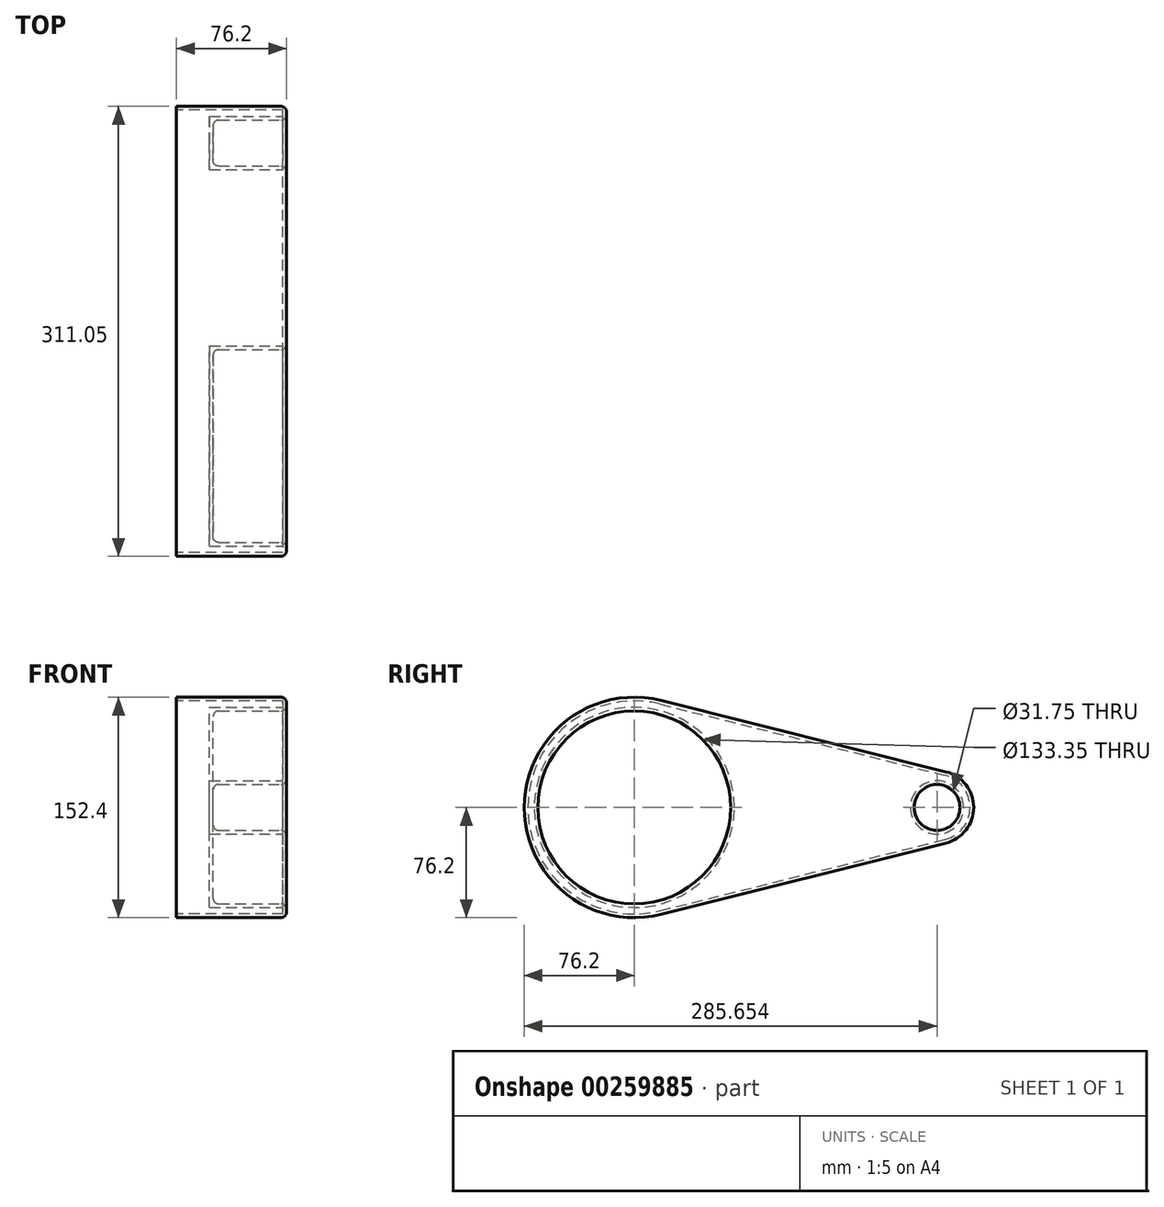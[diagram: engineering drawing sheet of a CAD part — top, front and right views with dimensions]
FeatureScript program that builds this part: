
annotation { "Feature Type Name" : "Feature", "Feature Type Description" : "" }
export const myFeature = defineFeature(function(context is Context, id is Id, definition is map)
    precondition{}
    {
        {
            var Q0;
            Q0=qCreatedBy(makeId("Right.planeOp"),FACE);
            var sketch = newSketch(context, id + "F0", { "sketchPlane" : qUnion([Q0])});
            skCircle(sketch, "E0", {"center": v(0, 0) * mm, "radius": 76.2 * mm});
            skCircle(sketch, "E1", {"center": v(209.45, 0) * mm, "radius": 25.4 * mm});
            skLineSegment(sketch, "E2", {"start": v(18.48, 73.92) * mm, "end": v(215.61, 24.64) * mm});
            skLineSegment(sketch, "E3", {"start": v(215.61, 24.64) * mm, "end": v(210.17, 25.39) * mm});
            skLineSegment(sketch, "E4", {"start": v(18.48, -73.92) * mm, "end": v(215.61, -24.64) * mm});
            skSolve(sketch);
        }
        {
            var Q0;
            Q0 = qSketchRegion(id + "F0", true);
            extrude(context, id + "F1", {"entities" : qUnion([Q0]), "depth" : 76.2 * mm});
        }
        {
            var Q0;
            Q0=makeQuery(id+"F1.opExtrude","CAP_FACE",FACE,{"disambiguationData":[OSD([sQuery(id+"F0.wireOp",EDGE,"E0"),sQuery(id+"F0.wireOp",EDGE,"E1"),sQuery(id+"F0.wireOp",EDGE,"E2"),sQuery(id+"F0.wireOp",EDGE,"E4")])],"isStart":false});
            var sketch = newSketch(context, id + "F2", { "sketchPlane" : qUnion([Q0])});
            skCircle(sketch, "E5", {"center": v(0, 0) * mm, "radius": 66.68 * mm});
            skCircle(sketch, "E6", {"center": v(209.45, 0) * mm, "radius": 15.88 * mm});
            skSolve(sketch);
        }
        {
            var Q0;
            Q0=makeQuery(id+"F2.imprint","IMPRINT",FACE,{"disambiguationData":[TD([[makeQuery(id+"F2.imprint","IMPRINT",EDGE,{"derivedFrom":sQuery(id+"F2.wireOp",EDGE,"E5")}),1.0]])]});
            var Q1;
            Q1=makeQuery(id+"F2.imprint","IMPRINT",FACE,{"disambiguationData":[TD([[makeQuery(id+"F2.imprint","IMPRINT",EDGE,{"derivedFrom":sQuery(id+"F2.wireOp",EDGE,"E6")}),1.0]])]});
            extrude(context, id + "F3", {"entities" : qUnion([Q0, Q1]), "operationType" : NewBodyOperationType.REMOVE, "oppositeDirection" : true, "depth" : 50.8 * mm});
        }
        {
            var Q0;
            Q0=makeQuery(id+"F1.opExtrude","CAP_FACE",FACE,{"disambiguationData":[OSD([sQuery(id+"F0.wireOp",EDGE,"E0"),sQuery(id+"F0.wireOp",EDGE,"E1"),sQuery(id+"F0.wireOp",EDGE,"E2"),sQuery(id+"F0.wireOp",EDGE,"E4")])],"isStart":true});
            shell(context, id + "F4", {"entities" : qUnion([Q0]), "thickness" : 2.54 * mm});
        }
        {
            var Q0;
            Q0=makeQuery(id+"F1.opExtrude","CAP_FACE",FACE,{"disambiguationData":[OSD([sQuery(id+"F0.wireOp",EDGE,"E0"),sQuery(id+"F0.wireOp",EDGE,"E1"),sQuery(id+"F0.wireOp",EDGE,"E2"),sQuery(id+"F0.wireOp",EDGE,"E4")])],"isStart":false});
            fillet(context, id + "F5", {"entities" : qUnion([Q0]), "radius" : 3.8 * mm, "tangentPropagation" : true, "allowEdgeOverflow" : false});
        }
        {
            var Q0;
            Q0=makeQuery(id+"F3.boolean.opBoolean","COPY",FACE,{"derivedFrom":makeQuery(id+"F3.opExtrude","CAP_FACE",FACE,{"disambiguationData":[OSD([sQuery(id+"F2.wireOp",EDGE,"E5")])],"isStart":false})});
            var Q1;
            Q1=makeQuery(id+"F3.boolean.opBoolean","COPY",FACE,{"derivedFrom":makeQuery(id+"F3.opExtrude","CAP_FACE",FACE,{"disambiguationData":[OSD([sQuery(id+"F2.wireOp",EDGE,"E6")])],"isStart":false})});
            var Q2;
            Q2=makeQuery(id+"F3.boolean.opBoolean","COPY",EDGE,{"derivedFrom":makeQuery(id+"F3.opExtrude","CAP_EDGE",EDGE,{"disambiguationData":[OSD([sQuery(id+"F2.wireOp",EDGE,"E6")])],"isStart":false})});
            var Q3;
            Q3=makeQuery(id+"F3.boolean.opBoolean","COPY",EDGE,{"derivedFrom":makeQuery(id+"F3.opExtrude","CAP_EDGE",EDGE,{"disambiguationData":[OSD([sQuery(id+"F2.wireOp",EDGE,"E5")])],"isStart":false})});
            fillet(context, id + "F6", {"entities" : qUnion([Q0, Q1, Q2, Q3]), "radius" : 3.8 * mm, "tangentPropagation" : true, "allowEdgeOverflow" : false});
        }
    });
